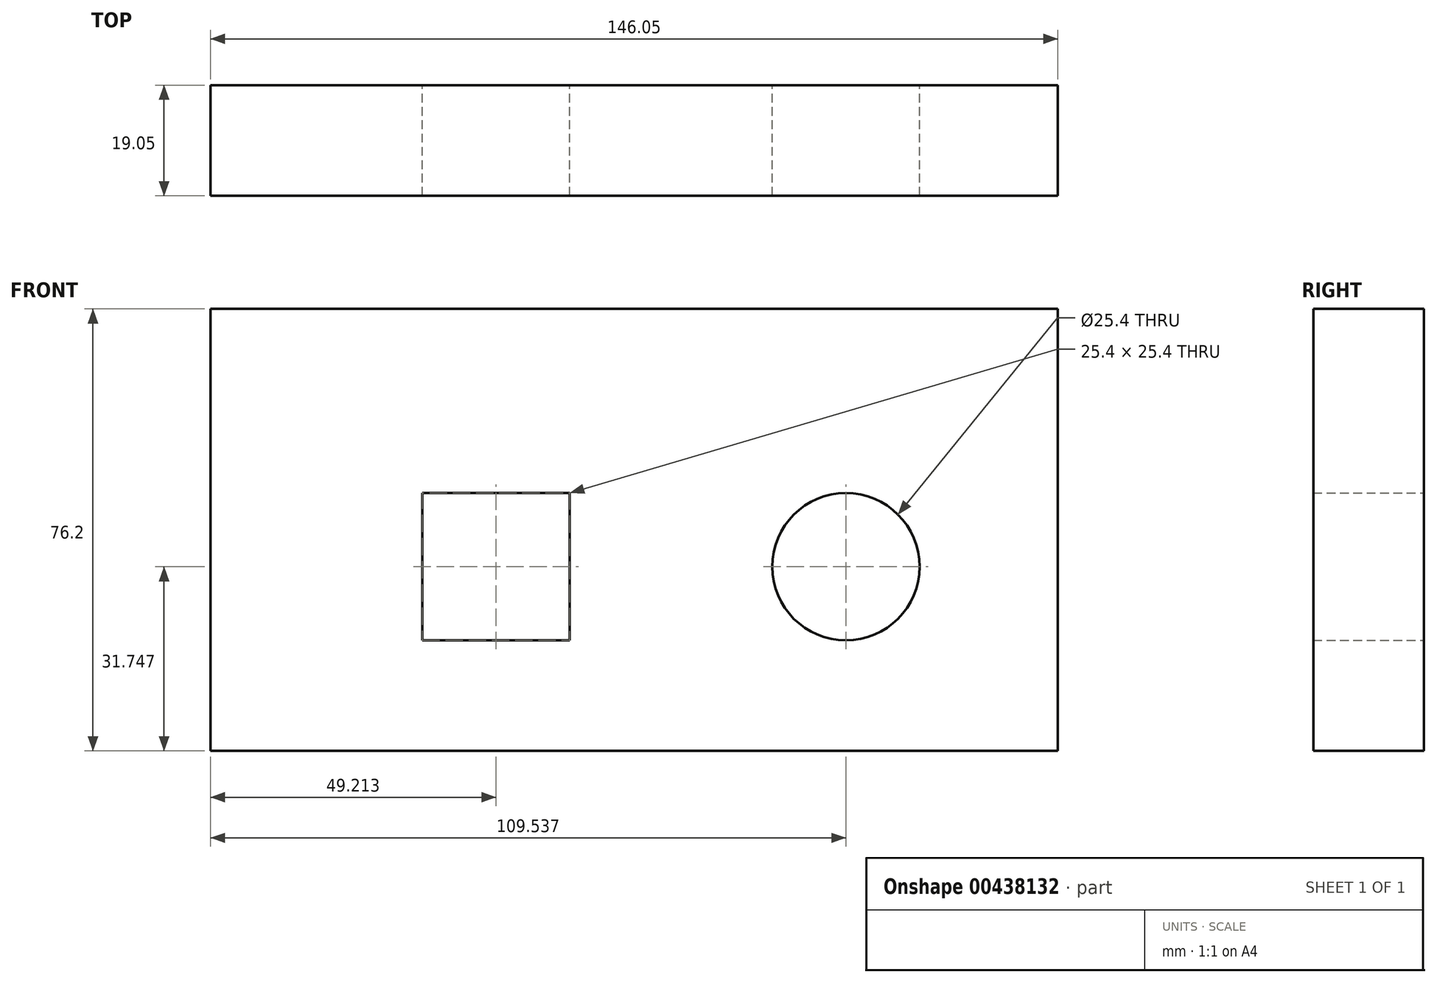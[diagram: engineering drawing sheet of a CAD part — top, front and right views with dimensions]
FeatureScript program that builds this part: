
annotation { "Feature Type Name" : "Feature", "Feature Type Description" : "" }
export const myFeature = defineFeature(function(context is Context, id is Id, definition is map)
    precondition{}
    {
        {
            var Q0;
            Q0=qCreatedBy(makeId("Front.planeOp"),FACE);
            var sketch = newSketch(context, id + "F0", { "sketchPlane" : qUnion([Q0])});
            skLineSegment(sketch, "E0", {"start": v(-85.93, 39.34) * mm, "end": v(60.12, 39.34) * mm});
            skLineSegment(sketch, "E1", {"start": v(60.12, 39.34) * mm, "end": v(60.12, -36.86) * mm});
            skLineSegment(sketch, "E2", {"start": v(60.12, -36.86) * mm, "end": v(-85.93, -36.86) * mm});
            skLineSegment(sketch, "E3", {"start": v(-85.93, -36.86) * mm, "end": v(-85.93, 39.34) * mm});
            skCircle(sketch, "E4", {"center": v(23.6, -5.11) * mm, "radius": 12.7 * mm});
            skLineSegment(sketch, "E5.bottom", {"start": v(-49.42, 7.59) * mm, "end": v(-24.02, 7.59) * mm});
            skLineSegment(sketch, "E5.top", {"start": v(-49.42, -17.81) * mm, "end": v(-24.02, -17.81) * mm});
            skLineSegment(sketch, "E5.left", {"start": v(-49.42, 7.59) * mm, "end": v(-49.42, -17.81) * mm});
            skLineSegment(sketch, "E5.right", {"start": v(-24.02, 7.59) * mm, "end": v(-24.02, -17.81) * mm});
            skPoint(sketch, "E6", {"position": v(-24.02, -5.11) * mm});
            skSolve(sketch);
        }
        {
            var Q0;
            Q0 = qSketchRegion(id + "F0", true);
            extrude(context, id + "F1", {"entities" : qUnion([Q0]), "depth" : 19.05 * mm});
        }
    });
